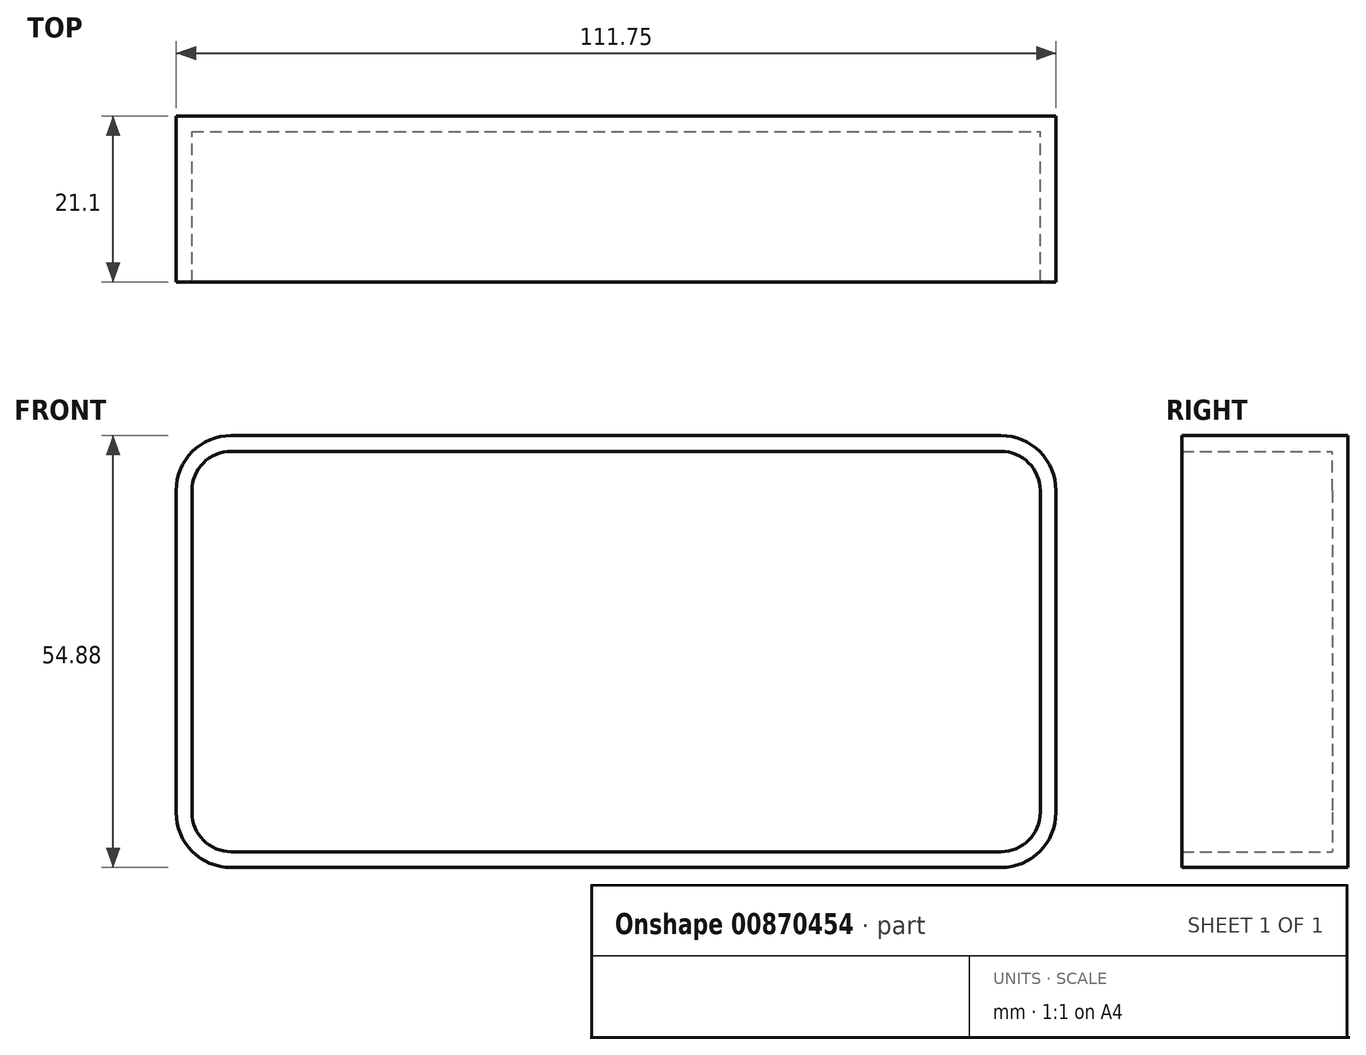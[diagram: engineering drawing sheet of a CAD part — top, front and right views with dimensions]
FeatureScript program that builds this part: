
annotation { "Feature Type Name" : "Feature", "Feature Type Description" : "" }
export const myFeature = defineFeature(function(context is Context, id is Id, definition is map)
    precondition{}
    {
        {
            var Q0;
            Q0=qCreatedBy(makeId("Front.planeOp"),FACE);
            var sketch = newSketch(context, id + "F0", { "sketchPlane" : qUnion([Q0])});
            skLineSegment(sketch, "E0.bottom", {"start": v(-56.22, 25.6) * mm, "end": v(41.53, 25.6) * mm});
            skLineSegment(sketch, "E0.top", {"start": v(-56.22, -25.28) * mm, "end": v(41.53, -25.28) * mm});
            skLineSegment(sketch, "E0.left", {"start": v(-61.22, 20.6) * mm, "end": v(-61.22, -20.28) * mm});
            skLineSegment(sketch, "E0.right", {"start": v(46.53, 20.6) * mm, "end": v(46.53, -20.28) * mm});
            skPoint(sketch, "E1.visualSharp", {"position": v(-61.22, 25.6) * mm});
            skArc(sketch, "E1.filletArc", {"start": v(-56.22, 25.6) * mm, "mid": v(-59.76, 24.14) * mm, "end": v(-61.22, 20.6) * mm});
            skPoint(sketch, "E2.visualSharp", {"position": v(46.53, -25.28) * mm});
            skArc(sketch, "E2.filletArc", {"start": v(41.53, -25.28) * mm, "mid": v(45.07, -23.82) * mm, "end": v(46.53, -20.28) * mm});
            skPoint(sketch, "E3.visualSharp", {"position": v(-61.22, -25.28) * mm});
            skArc(sketch, "E3.filletArc", {"start": v(-61.22, -20.28) * mm, "mid": v(-59.76, -23.82) * mm, "end": v(-56.22, -25.28) * mm});
            skPoint(sketch, "E4.visualSharp", {"position": v(46.53, 25.6) * mm});
            skArc(sketch, "E4.filletArc", {"start": v(46.53, 20.6) * mm, "mid": v(45.07, 24.14) * mm, "end": v(41.53, 25.6) * mm});
            skSolve(sketch);
        }
        {
            var Q0;
            Q0 = qSketchRegion(id + "F0", true);
            extrude(context, id + "F1", {"entities" : qUnion([Q0]), "depth" : 19.1 * mm, "offsetDistance" : 25 * mm});
        }
        {
            var Q0;
            Q0=makeQuery(id+"F1.opExtrude","CAP_FACE",FACE,{"disambiguationData":[OSD([sQuery(id+"F0.wireOp",EDGE,"E0.bottom"),sQuery(id+"F0.wireOp",EDGE,"E0.top"),sQuery(id+"F0.wireOp",EDGE,"E0.left"),sQuery(id+"F0.wireOp",EDGE,"E0.right"),sQuery(id+"F0.wireOp",EDGE,"E1.filletArc"),sQuery(id+"F0.wireOp",EDGE,"E2.filletArc"),sQuery(id+"F0.wireOp",EDGE,"E3.filletArc"),sQuery(id+"F0.wireOp",EDGE,"E4.filletArc")])],"isStart":false});
            shell(context, id + "F2", {"entities" : qUnion([Q0]), "thickness" : 2 * mm, "oppositeDirection" : true});
        }
    });
